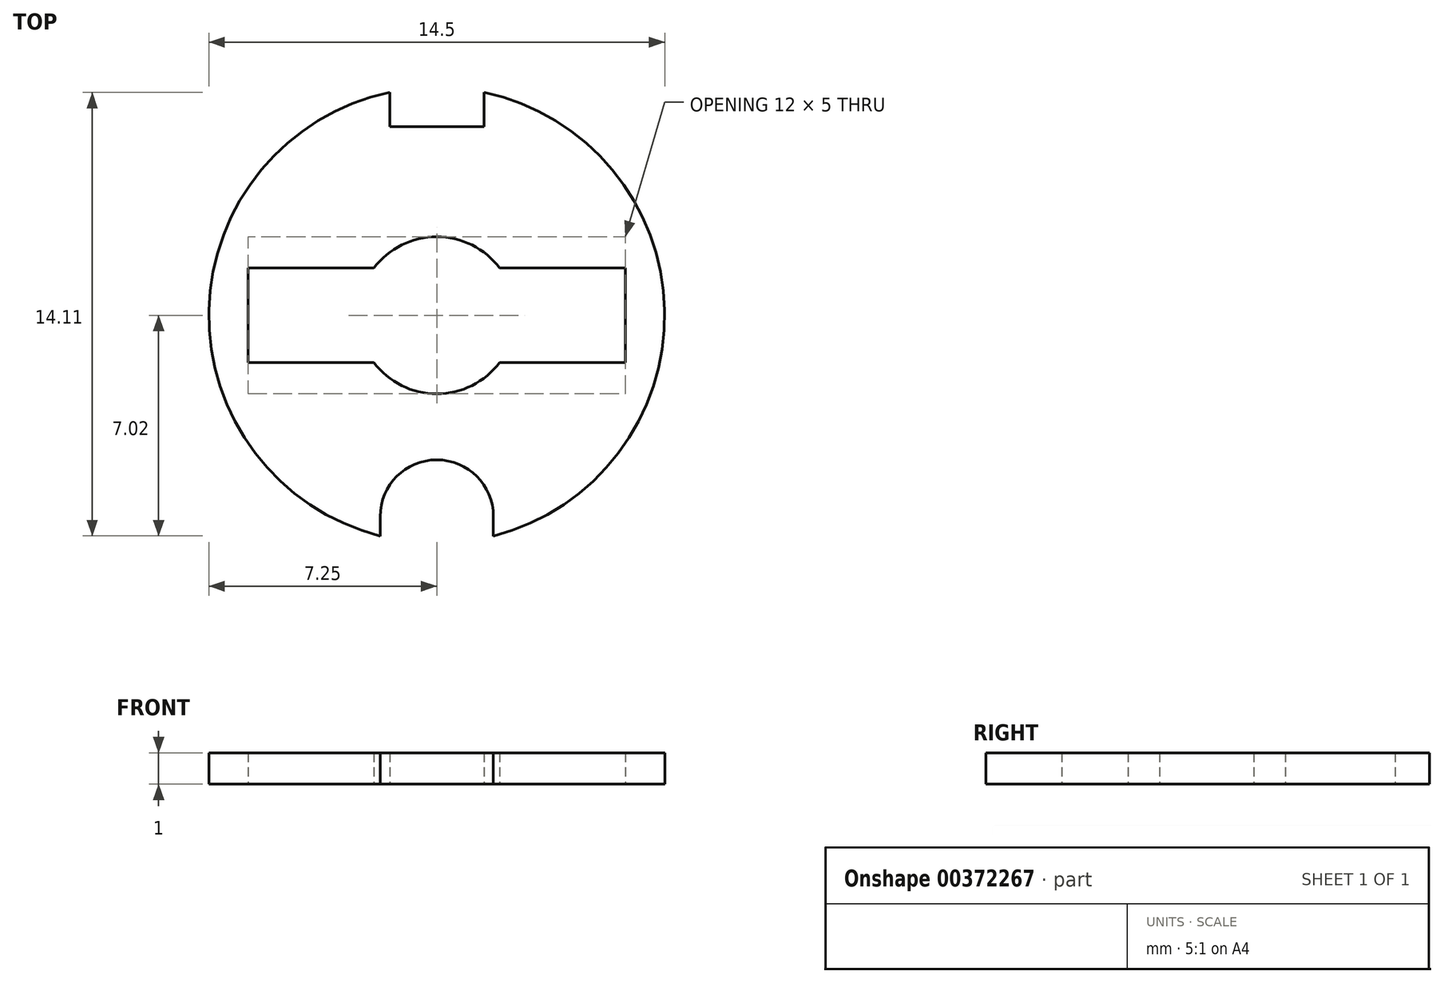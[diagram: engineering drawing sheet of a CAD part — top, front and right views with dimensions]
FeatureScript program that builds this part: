
annotation { "Feature Type Name" : "Feature", "Feature Type Description" : "" }
export const myFeature = defineFeature(function(context is Context, id is Id, definition is map)
    precondition{}
    {
        {
            var Q0;
            Q0=qCreatedBy(makeId("Top.planeOp"),FACE);
            var sketch = newSketch(context, id + "F0", { "sketchPlane" : qUnion([Q0])});
            skArc(sketch, "E0", {"start": v(1.8, -7.02) * mm, "mid": v(7.25, 0.15) * mm, "end": v(1.5, 7.1) * mm});
            skArc(sketch, "E1", {"start": v(-2, -1.5) * mm, "mid": v(0, -2.5) * mm, "end": v(2, -1.5) * mm});
            skLineSegment(sketch, "E2.bottom", {"start": v(-6, 1.5) * mm, "end": v(-2, 1.5) * mm});
            skLineSegment(sketch, "E2.top", {"start": v(-6, -1.5) * mm, "end": v(-2, -1.5) * mm});
            skLineSegment(sketch, "E2.left", {"start": v(-6, 1.5) * mm, "end": v(-6, -1.5) * mm});
            skLineSegment(sketch, "E2.right", {"start": v(6, 1.5) * mm, "end": v(6, -1.5) * mm});
            skPoint(sketch, "E3", {"position": v(6, 0) * mm});
            skPoint(sketch, "E4", {"position": v(0, 1.5) * mm});
            skLineSegment(sketch, "E5", {"start": v(-1.5, 6) * mm, "end": v(1.5, 6) * mm});
            skPoint(sketch, "E6", {"position": v(0, 6) * mm});
            skLineSegment(sketch, "E7", {"start": v(-1.5, 6) * mm, "end": v(-1.5, 7.1) * mm});
            skLineSegment(sketch, "E8", {"start": v(1.5, 6) * mm, "end": v(1.5, 7.1) * mm});
            skArc(sketch, "E9", {"start": v(1.8, -6.4) * mm, "mid": v(0, -4.6) * mm, "end": v(-1.8, -6.4) * mm});
            skLineSegment(sketch, "E10", {"start": v(-1.8, -6.4) * mm, "end": v(-1.8, -7.02) * mm});
            skLineSegment(sketch, "E11", {"start": v(1.8, -6.4) * mm, "end": v(1.8, -7.02) * mm});
            skArc(sketch, "E12.trimOffspring", {"start": v(-1.5, 7.1) * mm, "mid": v(-7.25, 0.15) * mm, "end": v(-1.8, -7.02) * mm});
            skLineSegment(sketch, "E13.trimOffspring", {"start": v(2, 1.5) * mm, "end": v(6, 1.5) * mm});
            skLineSegment(sketch, "E14.trimOffspring", {"start": v(2, -1.5) * mm, "end": v(6, -1.5) * mm});
            skArc(sketch, "E15.trimOffspring", {"start": v(2, 1.5) * mm, "mid": v(0, 2.5) * mm, "end": v(-2, 1.5) * mm});
            skSolve(sketch);
        }
        {
            var Q0;
            Q0=makeQuery(id+"F0.imprint","IMPRINT",FACE,{"disambiguationData":[TD([[makeQuery(id+"F0.imprint","IMPRINT",EDGE,{"derivedFrom":sQuery(id+"F0.wireOp",EDGE,"E0")}),1.0]])]});
            extrude(context, id + "F1", {"entities" : qUnion([Q0]), "depth" : 1 * mm});
        }
    });
